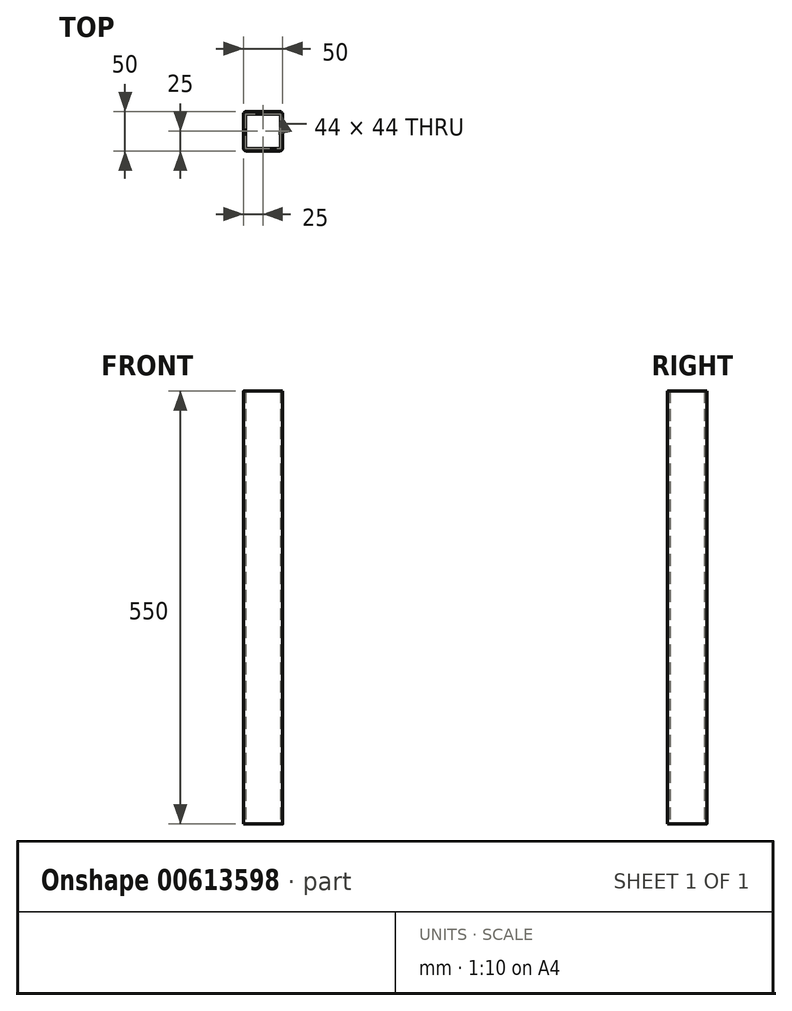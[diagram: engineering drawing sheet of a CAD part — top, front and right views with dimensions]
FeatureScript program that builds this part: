
annotation { "Feature Type Name" : "Feature", "Feature Type Description" : "" }
export const myFeature = defineFeature(function(context is Context, id is Id, definition is map)
    precondition{}
    {
        {
            var Q0;
            Q0=qCreatedBy(makeId("Top.planeOp"),FACE);
            var sketch = newSketch(context, id + "F0", { "sketchPlane" : qUnion([Q0])});
            skLineSegment(sketch, "E0.bottom", {"start": v(4, 0) * mm, "end": v(46, 0) * mm});
            skLineSegment(sketch, "E0.top", {"start": v(4, 50) * mm, "end": v(46, 50) * mm});
            skLineSegment(sketch, "E0.left", {"start": v(0, 4) * mm, "end": v(0, 46) * mm});
            skLineSegment(sketch, "E0.right", {"start": v(50, 4) * mm, "end": v(50, 46) * mm});
            skPoint(sketch, "E1.visualSharp", {"position": v(50, 0) * mm});
            skArc(sketch, "E1.filletArc", {"start": v(46, 0) * mm, "mid": v(48.83, 1.17) * mm, "end": v(50, 4) * mm});
            skPoint(sketch, "E2.visualSharp", {"position": v(50, 50) * mm});
            skArc(sketch, "E2.filletArc", {"start": v(50, 46) * mm, "mid": v(48.83, 48.83) * mm, "end": v(46, 50) * mm});
            skPoint(sketch, "E3.visualSharp", {"position": v(0, 50) * mm});
            skArc(sketch, "E3.filletArc", {"start": v(4, 50) * mm, "mid": v(1.17, 48.83) * mm, "end": v(0, 46) * mm});
            skPoint(sketch, "E4.visualSharp", {"position": v(0, 0) * mm});
            skArc(sketch, "E4.filletArc", {"start": v(0, 4) * mm, "mid": v(1.17, 1.17) * mm, "end": v(4, 0) * mm});
            skLineSegment(sketch, "E5.0", {"start": v(3, 47) * mm, "end": v(47, 47) * mm});
            skLineSegment(sketch, "E5.1", {"start": v(3, 3) * mm, "end": v(3, 47) * mm});
            skLineSegment(sketch, "E5.2", {"start": v(3, 3) * mm, "end": v(47, 3) * mm});
            skLineSegment(sketch, "E5.3", {"start": v(47, 3) * mm, "end": v(47, 47) * mm});
            skSolve(sketch);
        }
        {
            var Q0;
            Q0=qSketchRegion(id+"F0",true);
            extrude(context, id + "F1", {"entities" : qUnion([Q0]), "depth" : 550 * mm, "offsetDistance" : 25 * mm});
        }
    });
